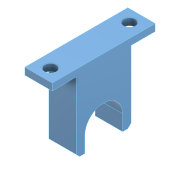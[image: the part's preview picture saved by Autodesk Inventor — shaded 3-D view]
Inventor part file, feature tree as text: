
AUTODESK INVENTOR PART (.ipt)
format: ipt  version: 2022 (Build 260153000, 153)  size: 137,216 bytes
history: native  units: mm
features: sketch x3, extrude x2, hole x1, chamfer x1, projected_geometry x1
ambient origin geometry x8: Origin, YZ Plane, XZ Plane, XY Plane, X Axis, Y Axis, Z Axis, Center Point
bodies: Solid1 (feature_tree)
feature tree (8):
  extrude  "Extrusion1"  Depth=2.5mm
  extrude  "Extrusion2"  Depth=18.0mm
  hole  "Hole1"  [1 undecoded]
  chamfer  "Chamfer1"  Distance=2.0mm
  sketch  "Sketch2"  dims[d2=2.5mm d3=9.0mm]
  sketch  "Sketch3"  dims[d4=1.0mm d5=18.0mm]
  sketch  "Sketch4"  dims[d6=8.0mm d7=0.0mm d8=7.0mm d9=2.0mm d10=0.0mm d11=3.4mm d12=6.0mm d13=6.0mm d14=2.0mm d15=90.0deg d16=8.0mm d17=20.594885mm d18=4.5mm d19=1.0mm d20=2.0mm d21=45.0deg]
  projected_geometry  "Project Cut Edges1"
note: 1 required parameter value undecoded (feature->parameter linkage not recoverable at this tier; creation-order binding heuristic only, values carry confidence <= 0.55)
